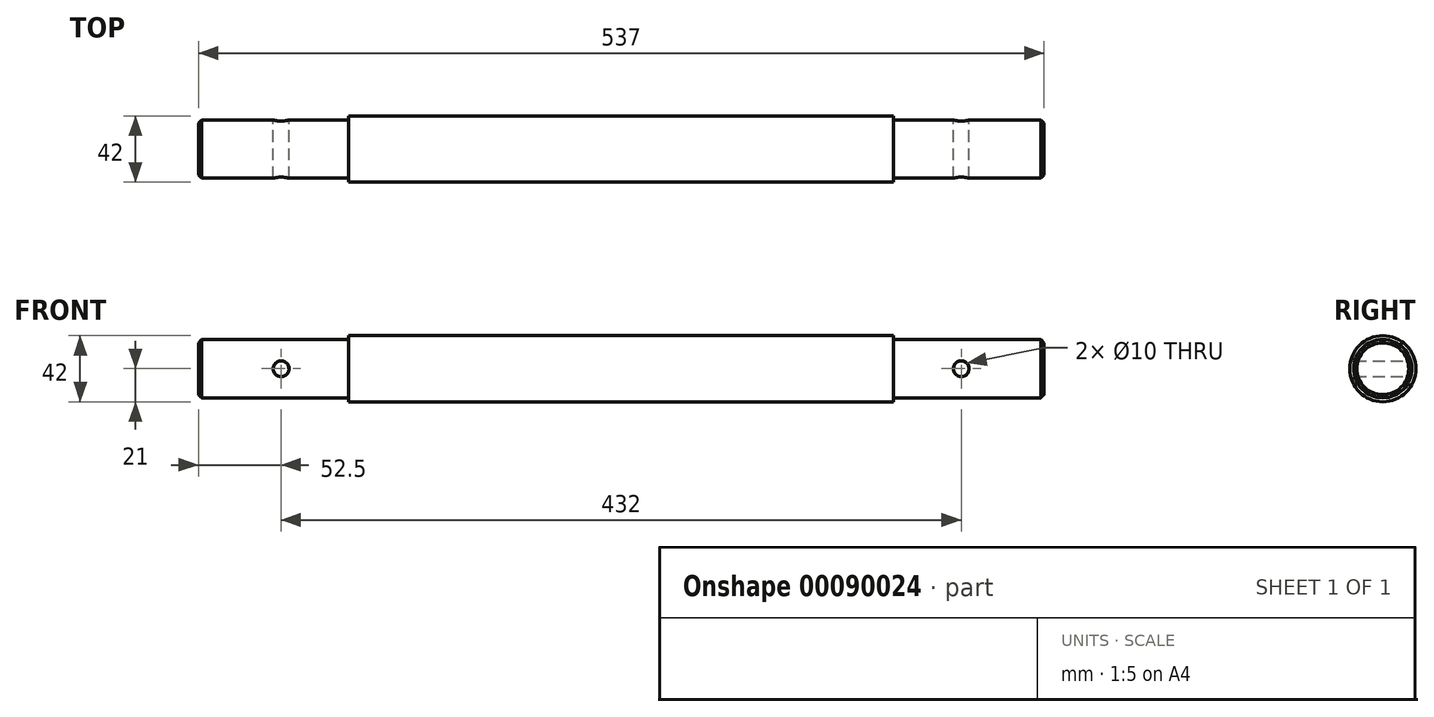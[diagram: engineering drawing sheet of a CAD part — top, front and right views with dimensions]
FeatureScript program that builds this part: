
annotation { "Feature Type Name" : "Feature", "Feature Type Description" : "" }
export const myFeature = defineFeature(function(context is Context, id is Id, definition is map)
    precondition{}
    {
        {
            var Q0;
            Q0=qCreatedBy(makeId("Right.planeOp"),FACE);
            var sketch = newSketch(context, id + "F0", { "sketchPlane" : qUnion([Q0])});
            skCircle(sketch, "E0", {"center": v(0, 0) * mm, "radius": 18.5 * mm});
            skSolve(sketch);
        }
        {
            var Q0;
            Q0=makeQuery(id+"F0.imprint","IMPRINT",FACE,{"disambiguationData":[TD([[makeQuery(id+"F0.imprint","IMPRINT",EDGE,{"derivedFrom":sQuery(id+"F0.wireOp",EDGE,"E0")}),1.0]])]});
            extrude(context, id + "F1", {"entities" : qUnion([Q0]), "depth" : 537 * mm, "symmetric" : true});
        }
        {
            var Q0;
            Q0=qCreatedBy(makeId("Front.planeOp"),FACE);
            var sketch = newSketch(context, id + "F2", { "sketchPlane" : qUnion([Q0])});
            skCircle(sketch, "E1", {"center": v(-216, 0) * mm, "radius": 5 * mm});
            skCircle(sketch, "E2", {"center": v(216, 0) * mm, "radius": 5 * mm});
            skSolve(sketch);
        }
        {
            var Q0;
            Q0 = qSketchRegion(id + "F2", true);
            extrude(context, id + "F3", {"entities" : qUnion([Q0]), "operationType" : NewBodyOperationType.REMOVE, "depth" : 50 * mm, "symmetric" : true});
        }
        {
            var Q0;
            Q0=makeQuery(id+"F1.opExtrude","CAP_EDGE",EDGE,{"disambiguationData":[OSD([sQuery(id+"F0.wireOp",EDGE,"E0")])],"isStart":true});
            var Q1;
            Q1=makeQuery(id+"F1.opExtrude","CAP_EDGE",EDGE,{"disambiguationData":[OSD([sQuery(id+"F0.wireOp",EDGE,"E0")])],"isStart":false});
            chamfer(context, id + "F4", {"entities" : qUnion([Q0, Q1]), "width" : 2 * mm, "tangentPropagation" : true});
        }
        {
            var Q0;
            Q0=qCreatedBy(makeId("Right.planeOp"),FACE);
            var sketch = newSketch(context, id + "F5", { "sketchPlane" : qUnion([Q0])});
            skCircle(sketch, "E3", {"center": v(0, 0) * mm, "radius": 21 * mm});
            skSolve(sketch);
        }
        {
            var Q0;
            Q0 = qSketchRegion(id + "F5", true);
            extrude(context, id + "F6", {"entities" : qUnion([Q0]), "operationType" : NewBodyOperationType.ADD, "depth" : 346 * mm, "symmetric" : true});
        }
    });
